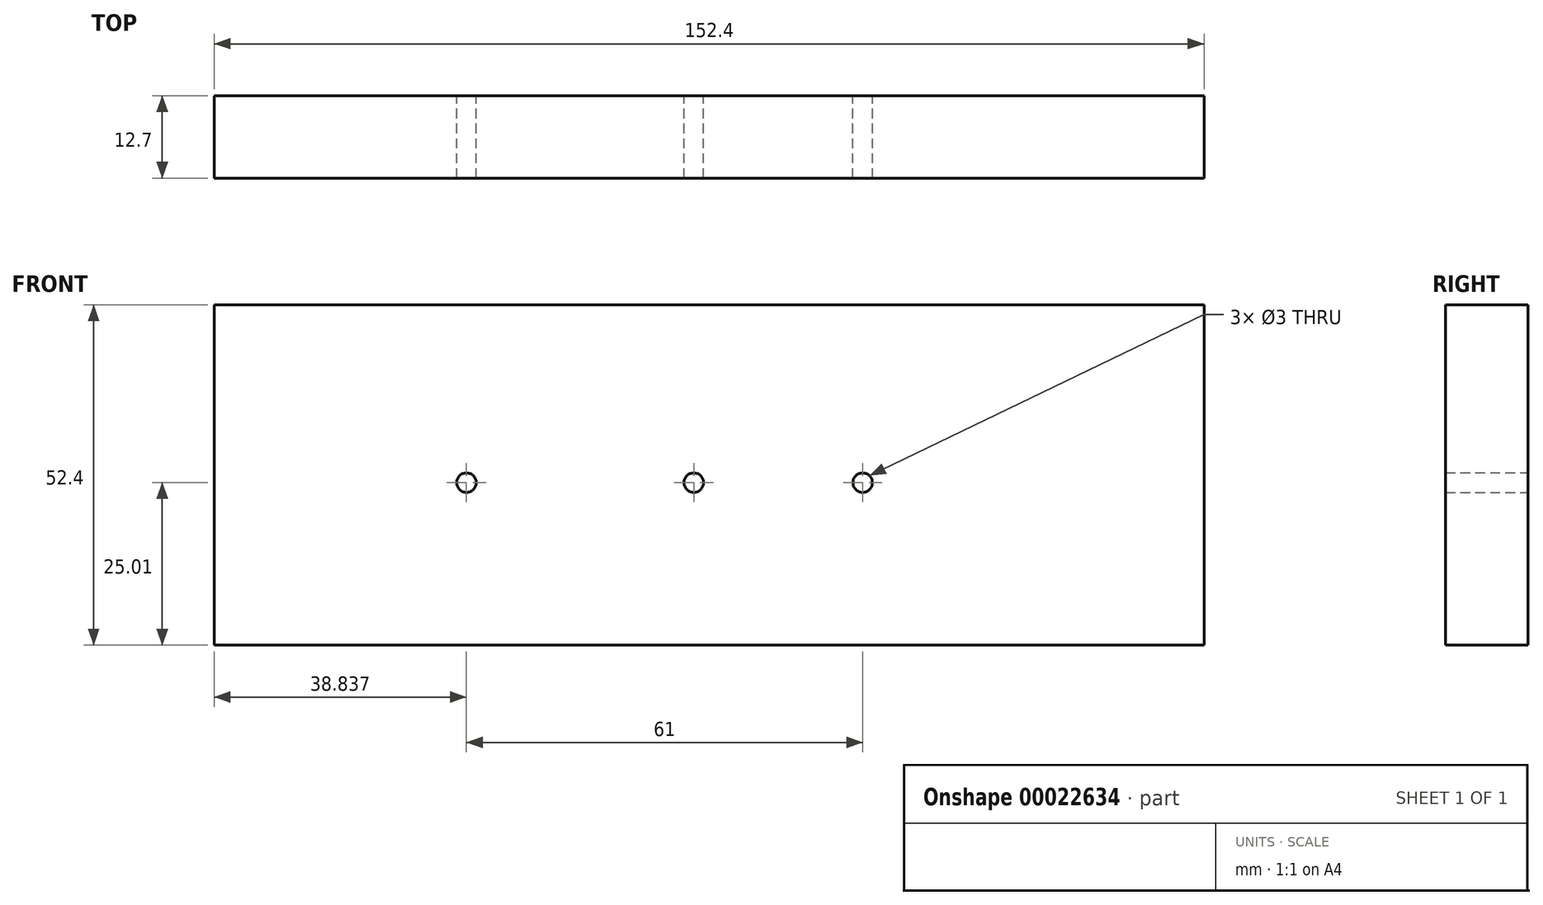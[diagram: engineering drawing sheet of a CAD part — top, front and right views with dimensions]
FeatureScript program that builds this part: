
annotation { "Feature Type Name" : "Feature", "Feature Type Description" : "" }
export const myFeature = defineFeature(function(context is Context, id is Id, definition is map)
    precondition{}
    {
        {
            var Q0;
            Q0=qCreatedBy(makeId("Front.planeOp"),FACE);
            var sketch = newSketch(context, id + "F0", { "sketchPlane" : qUnion([Q0])});
            skLineSegment(sketch, "E0.bottom", {"start": v(-75.57, -25) * mm, "end": v(76.83, -25) * mm});
            skLineSegment(sketch, "E0.top", {"start": v(-75.57, 27.39) * mm, "end": v(76.83, 27.39) * mm});
            skLineSegment(sketch, "E0.left", {"start": v(-75.57, -25) * mm, "end": v(-75.57, 27.39) * mm});
            skLineSegment(sketch, "E0.right", {"start": v(76.83, -25) * mm, "end": v(76.83, 27.39) * mm});
            skCircle(sketch, "E1", {"center": v(-36.73, 0) * mm, "radius": 1.5 * mm});
            skCircle(sketch, "E2", {"center": v(-1.73, 0) * mm, "radius": 1.5 * mm});
            skPoint(sketch, "E3.orphan", {"position": v(-7.17, 0) * mm});
            skPoint(sketch, "E4.end.orphan", {"position": v(-1.73, -34.04) * mm});
            skPoint(sketch, "E4.start.orphan", {"position": v(-36.73, -34.04) * mm});
            skCircle(sketch, "E5", {"center": v(24.27, 0) * mm, "radius": 1.5 * mm});
            skPoint(sketch, "E6.start.orphan", {"position": v(-1.73, -63) * mm});
            skSolve(sketch);
        }
        {
            var Q0;
            Q0=makeQuery(id+"F0.imprint","IMPRINT",FACE,{"disambiguationData":[TD([[makeQuery(id+"F0.imprint","IMPRINT",EDGE,{"derivedFrom":sQuery(id+"F0.wireOp",EDGE,"E0.bottom")}),1.0]])]});
            extrude(context, id + "F1", {"entities" : qUnion([Q0]), "depth" : 12.7 * mm});
        }
    });
